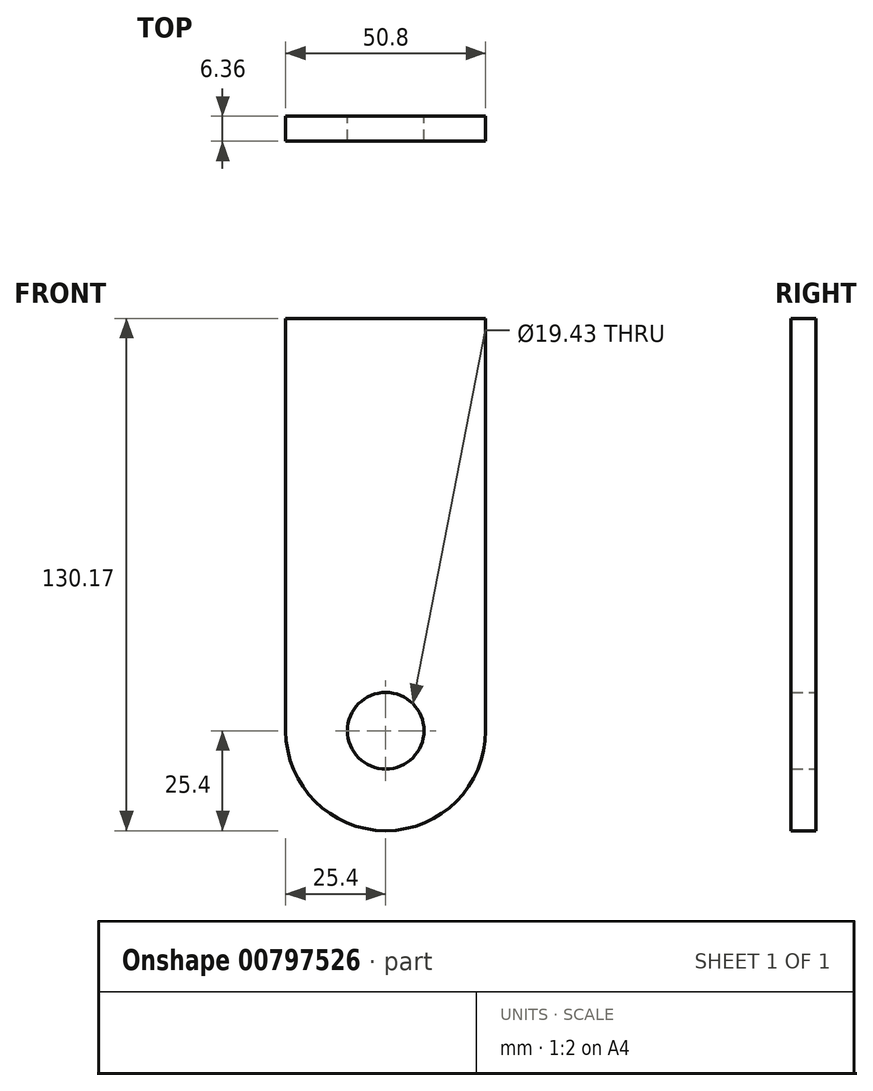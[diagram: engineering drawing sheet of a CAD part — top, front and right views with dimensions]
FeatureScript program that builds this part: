
annotation { "Feature Type Name" : "Feature", "Feature Type Description" : "" }
export const myFeature = defineFeature(function(context is Context, id is Id, definition is map)
    precondition{}
    {
        {
            var Q0;
            Q0=qCreatedBy(makeId("Front.planeOp"),FACE);
            var sketch = newSketch(context, id + "F0", { "sketchPlane" : qUnion([Q0])});
            skCircle(sketch, "E0", {"center": v(0, 0) * mm, "radius": 9.72 * mm});
            skArc(sketch, "E1", {"start": v(-25.4, 0) * mm, "mid": v(0, -25.4) * mm, "end": v(25.4, 0) * mm});
            skLineSegment(sketch, "E2.bottom", {"start": v(-25.4, 104.78) * mm, "end": v(25.4, 104.78) * mm});
            skLineSegment(sketch, "E2.left", {"start": v(-25.4, 104.78) * mm, "end": v(-25.4, 0) * mm});
            skLineSegment(sketch, "E2.right", {"start": v(25.4, 104.78) * mm, "end": v(25.4, 0) * mm});
            skSolve(sketch);
        }
        {
            var Q0;
            Q0 = qSketchRegion(id + "F0", true);
            extrude(context, id + "F1", {"entities" : qUnion([Q0]), "endBound" : BoundingType.SYMMETRIC, "depth" : 6.35 * mm, "offsetDistance" : 25.4 * mm});
        }
    });
